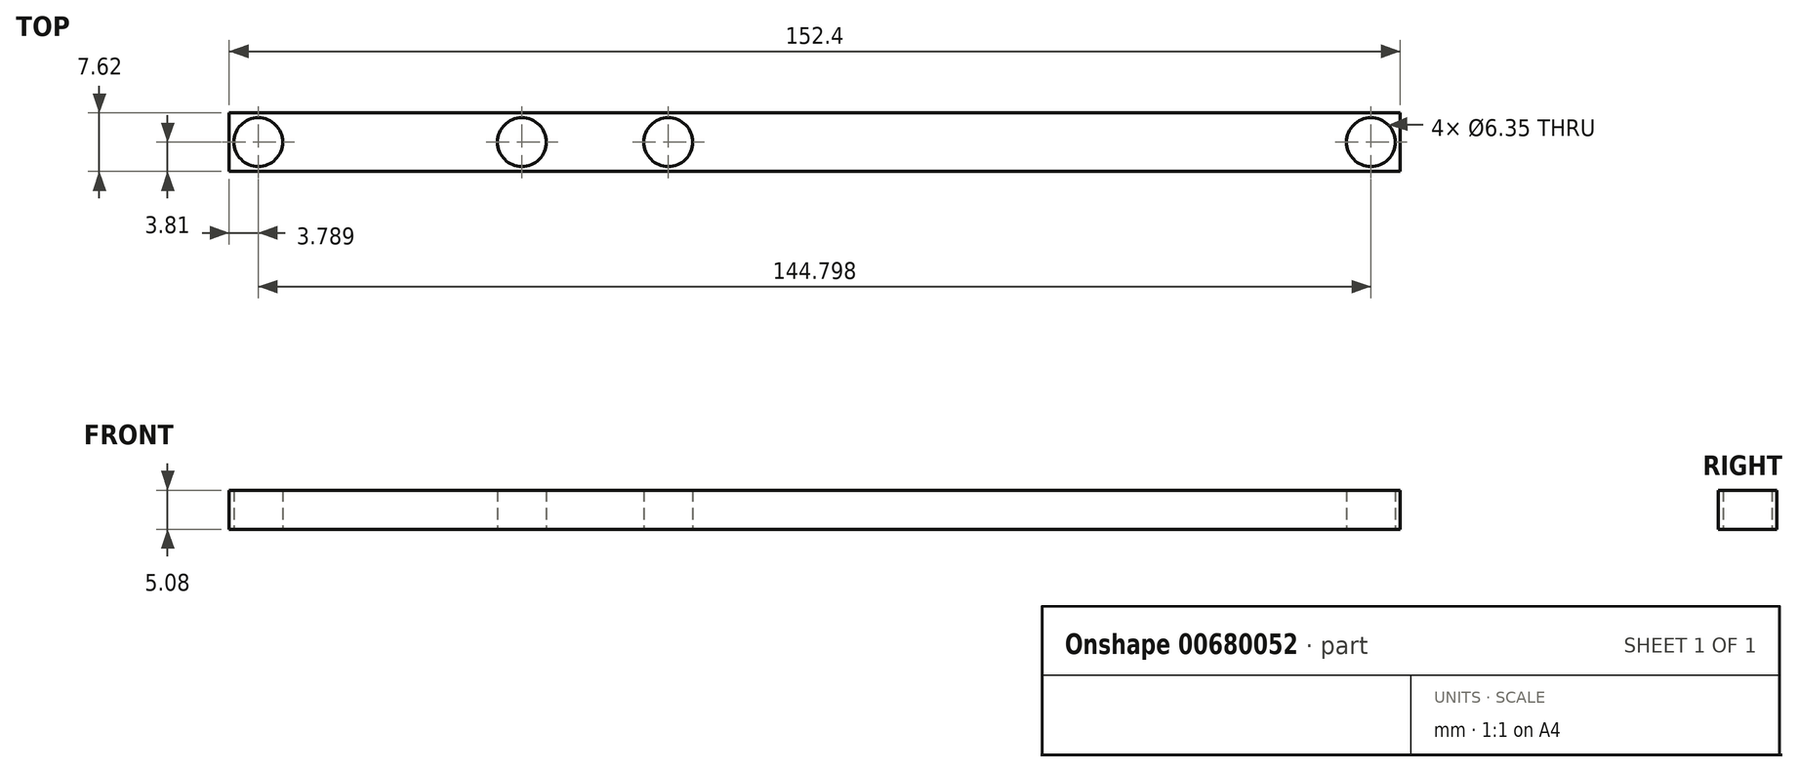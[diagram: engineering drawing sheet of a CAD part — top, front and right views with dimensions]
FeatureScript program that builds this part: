
annotation { "Feature Type Name" : "Feature", "Feature Type Description" : "" }
export const myFeature = defineFeature(function(context is Context, id is Id, definition is map)
    precondition{}
    {
        {
            var Q0;
            Q0=qCreatedBy(makeId("Top.planeOp"),FACE);
            var sketch = newSketch(context, id + "F0", { "sketchPlane" : qUnion([Q0])});
            skLineSegment(sketch, "E0.bottom", {"start": v(76.2, -3.8) * mm, "end": v(-76.2, -3.81) * mm});
            skLineSegment(sketch, "E0.top", {"start": v(76.2, 3.81) * mm, "end": v(-76.2, 3.8) * mm});
            skLineSegment(sketch, "E0.left", {"start": v(76.2, -3.8) * mm, "end": v(76.2, 3.81) * mm});
            skLineSegment(sketch, "E0.right", {"start": v(-76.2, -3.81) * mm, "end": v(-76.2, 3.8) * mm});
            skPoint(sketch, "E0.middle", {"position": v(0, 0) * mm});
            skCircle(sketch, "E1", {"center": v(-72.41, 0) * mm, "radius": 3.18 * mm});
            skCircle(sketch, "E2", {"center": v(72.39, 0) * mm, "radius": 3.18 * mm});
            skCircle(sketch, "E3", {"center": v(-38.1, 0) * mm, "radius": 3.18 * mm});
            skCircle(sketch, "E4", {"center": v(-19.05, 0) * mm, "radius": 3.18 * mm});
            skSolve(sketch);
        }
        {
            var Q0;
            Q0 = qSketchRegion(id + "F0", true);
            extrude(context, id + "F1", {"entities" : qUnion([Q0]), "depth" : 5.08 * mm, "offsetDistance" : 25.4 * mm});
        }
        {
            var Q0;
            Q0 = qSketchRegion(id + "F0", true);
            extrude(context, id + "F2", {"entities" : qUnion([Q0]), "depth" : 5.08 * mm, "offsetDistance" : 25.4 * mm});
        }
        {
            var Q0;
            Q0=makeQuery(id+"F1.opExtrude","SWEPT_BODY",BODY,{"disambiguationData":[OSD([sQuery(id+"F0.wireOp",EDGE,"E0.bottom"),sQuery(id+"F0.wireOp",EDGE,"E0.top"),sQuery(id+"F0.wireOp",EDGE,"E0.left"),sQuery(id+"F0.wireOp",EDGE,"E0.right"),sQuery(id+"F0.wireOp",EDGE,"E1"),sQuery(id+"F0.wireOp",EDGE,"E2"),sQuery(id+"F0.wireOp",EDGE,"E3"),sQuery(id+"F0.wireOp",EDGE,"E4")])]});
            deleteBodies(context, id + "F3", {"entities" : qUnion([Q0])});
        }
    });
